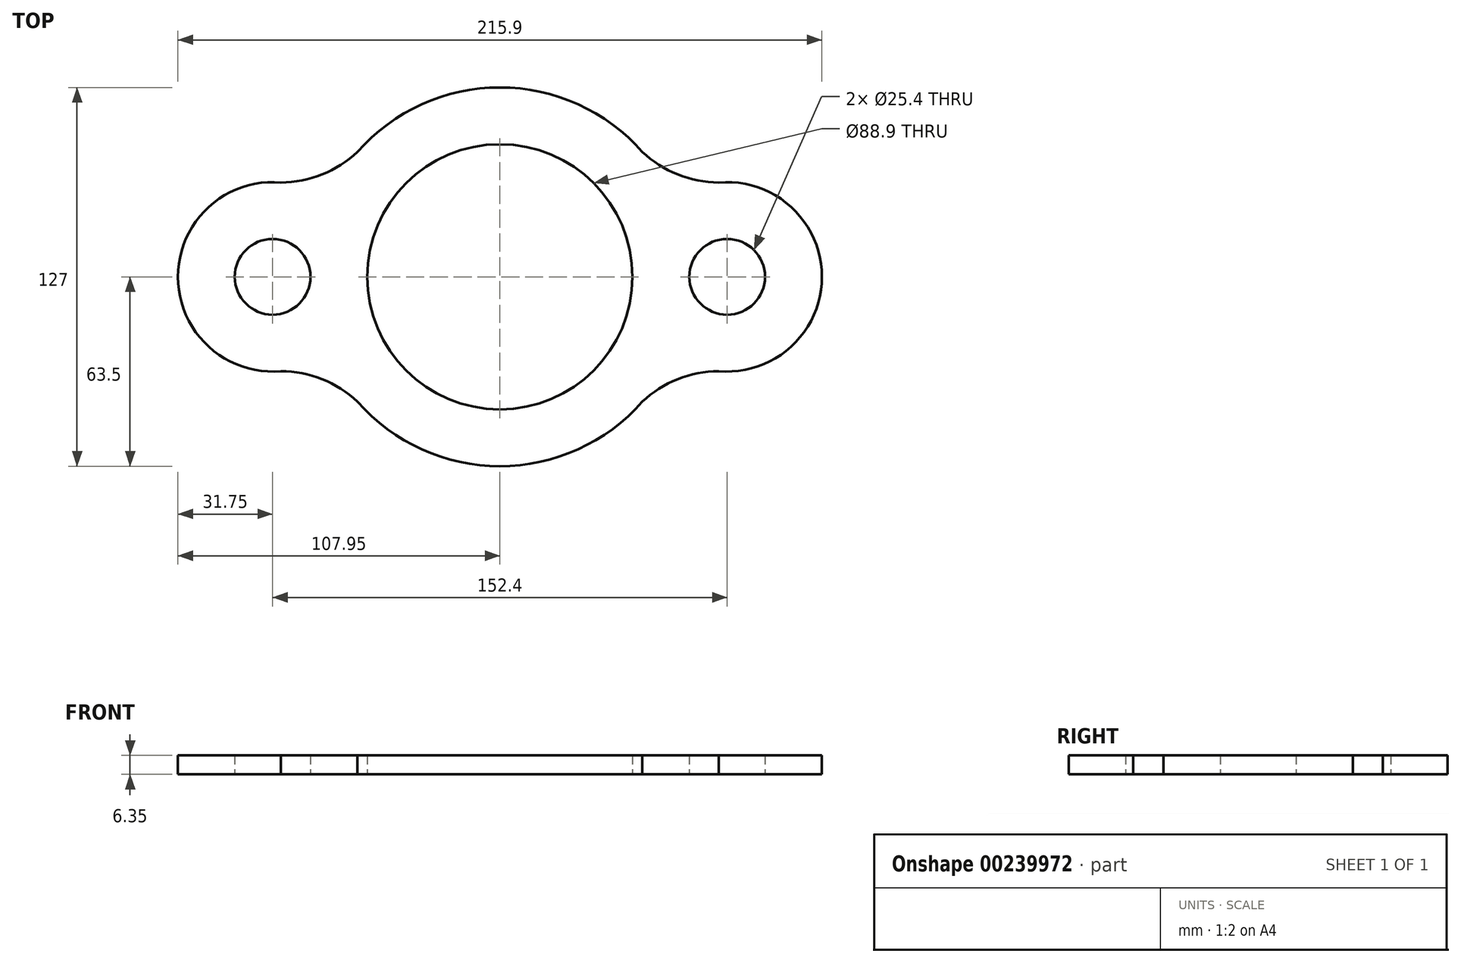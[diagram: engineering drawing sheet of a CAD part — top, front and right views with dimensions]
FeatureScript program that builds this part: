
annotation { "Feature Type Name" : "Feature", "Feature Type Description" : "" }
export const myFeature = defineFeature(function(context is Context, id is Id, definition is map)
    precondition{}
    {
        {
            var Q0;
            Q0=qCreatedBy(makeId("Top.planeOp"),FACE);
            var sketch = newSketch(context, id + "F0", { "sketchPlane" : qUnion([Q0])});
            skCircle(sketch, "E0", {"center": v(0, 0) * mm, "radius": 44.45 * mm});
            skCircle(sketch, "E1", {"center": v(0, 0) * mm, "radius": 63.5 * mm});
            skCircle(sketch, "E2", {"center": v(-76.2, 0) * mm, "radius": 12.7 * mm});
            skCircle(sketch, "E3", {"center": v(76.2, 0) * mm, "radius": 12.7 * mm});
            skCircle(sketch, "E4", {"center": v(76.2, 0) * mm, "radius": 31.75 * mm});
            skCircle(sketch, "E5", {"center": v(-76.2, 0) * mm, "radius": 31.75 * mm});
            skArc(sketch, "E6", {"start": v(73.38, -31.62) * mm, "mid": v(59.6, -34.34) * mm, "end": v(47.74, -41.87) * mm});
            skArc(sketch, "E7", {"start": v(-47.74, -41.87) * mm, "mid": v(-59.6, -34.34) * mm, "end": v(-73.38, -31.62) * mm});
            skArc(sketch, "E8", {"start": v(-73.38, 31.62) * mm, "mid": v(-59.6, 34.34) * mm, "end": v(-47.74, 41.87) * mm});
            skArc(sketch, "E9", {"start": v(47.74, 41.87) * mm, "mid": v(59.6, 34.34) * mm, "end": v(73.38, 31.62) * mm});
            skSolve(sketch);
        }
        {
            var Q0;
            {var subQ0=sQuery(id+"F0.wireOp",EDGE,"E2");Q0=makeQuery(id+"F0.imprint","IMPRINT",FACE,{"disambiguationData":[TD([[makeQuery(id+"F0.imprint","IMPRINT",EDGE,{"derivedFrom":subQ0}),-1.0]])]});}
            var Q1;
            {var subQ0=sQuery(id+"F0.wireOp",EDGE,"E1");var subQ1=makeQuery(id+"F0.imprint","INTERSECT",VERTEX,{"derivedFrom":[subQ0,sQuery(id+"F0.wireOp",EDGE,"E2")]});Q1=makeQuery(id+"F0.imprint","IMPRINT",FACE,{"disambiguationData":[TD([[makeQuery(id+"F0.imprint","IMPRINT",EDGE,{"disambiguationData":[TD([[subQ1,1.0]])],"derivedFrom":subQ0}),1.0]])]});}
            var Q2;
            {var subQ2=sQuery(id+"F0.wireOp",EDGE,"E4");var subQ6=sQuery(id+"F0.wireOp",EDGE,"E0");var subQ9=makeQuery(id+"F0.imprint","INTERSECT",VERTEX,{"derivedFrom":[subQ6,subQ2]});Q2=makeQuery(id+"F0.imprint","IMPRINT",FACE,{"disambiguationData":[TD([[makeQuery(id+"F0.imprint","IMPRINT",EDGE,{"disambiguationData":[TD([[subQ9,1.0]])],"derivedFrom":subQ6}),-1.0]])]});}
            var Q3;
            {var subQ0=sQuery(id+"F0.wireOp",EDGE,"E7");Q3=makeQuery(id+"F0.imprint","IMPRINT",FACE,{"disambiguationData":[TD([[makeQuery(id+"F0.imprint","IMPRINT",EDGE,{"derivedFrom":subQ0}),-1.0]])]});}
            var Q4;
            {var subQ0=sQuery(id+"F0.wireOp",EDGE,"E8");Q4=makeQuery(id+"F0.imprint","IMPRINT",FACE,{"disambiguationData":[TD([[makeQuery(id+"F0.imprint","IMPRINT",EDGE,{"derivedFrom":subQ0}),-1.0]])]});}
            var Q5;
            {var subQ5=sQuery(id+"F0.wireOp",EDGE,"E4");var subQ7=sQuery(id+"F0.wireOp",EDGE,"E0");var subQ8=makeQuery(id+"F0.imprint","INTERSECT",VERTEX,{"derivedFrom":[subQ7,subQ5]});Q5=makeQuery(id+"F0.imprint","IMPRINT",FACE,{"disambiguationData":[TD([[makeQuery(id+"F0.imprint","IMPRINT",EDGE,{"disambiguationData":[TD([[subQ8,-1.0]])],"derivedFrom":subQ7}),-1.0]])]});}
            var Q6;
            {var subQ5=sQuery(id+"F0.wireOp",EDGE,"E3");Q6=makeQuery(id+"F0.imprint","IMPRINT",FACE,{"disambiguationData":[TD([[makeQuery(id+"F0.imprint","IMPRINT",EDGE,{"derivedFrom":subQ5}),-1.0]])]});}
            var Q7;
            {var subQ0=sQuery(id+"F0.wireOp",EDGE,"E1");var subQ1=makeQuery(id+"F0.imprint","INTERSECT",VERTEX,{"derivedFrom":[subQ0,sQuery(id+"F0.wireOp",EDGE,"E3")]});Q7=makeQuery(id+"F0.imprint","IMPRINT",FACE,{"disambiguationData":[TD([[makeQuery(id+"F0.imprint","IMPRINT",EDGE,{"disambiguationData":[TD([[subQ1,-1.0]])],"derivedFrom":subQ0}),1.0]])]});}
            var Q8;
            {var subQ0=sQuery(id+"F0.wireOp",EDGE,"E9");Q8=makeQuery(id+"F0.imprint","IMPRINT",FACE,{"disambiguationData":[TD([[makeQuery(id+"F0.imprint","IMPRINT",EDGE,{"derivedFrom":subQ0}),-1.0]])]});}
            var Q9;
            {var subQ0=sQuery(id+"F0.wireOp",EDGE,"E6");Q9=makeQuery(id+"F0.imprint","IMPRINT",FACE,{"disambiguationData":[TD([[makeQuery(id+"F0.imprint","IMPRINT",EDGE,{"derivedFrom":subQ0}),-1.0]])]});}
            extrude(context, id + "F1", {"entities" : qUnion([Q0, Q1, Q2, Q3, Q4, Q5, Q6, Q7, Q8, Q9]), "depth" : 6.35 * mm});
        }
    });
